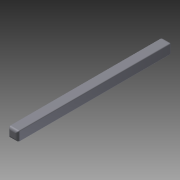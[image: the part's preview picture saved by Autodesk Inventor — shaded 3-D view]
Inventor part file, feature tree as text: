
AUTODESK INVENTOR PART (.ipt)
format: ipt  version: 2013 (Build 170138000, 138)  size: 186,880 bytes
history: native  units: mm (DEFAULTED — no unit token found)
features: plane x2, imported_body x1, other x1
ambient origin geometry x8: Origin, YZ Plane, XZ Plane, XY Plane, X Axis, Y Axis, Z Axis, Center Point
bodies: Solid1 (feature_tree)
feature tree (4):
  imported_body  "Base1"
  other  "Work Axis1"
  plane  "Work Plane1"
  plane  "Work Plane2"
